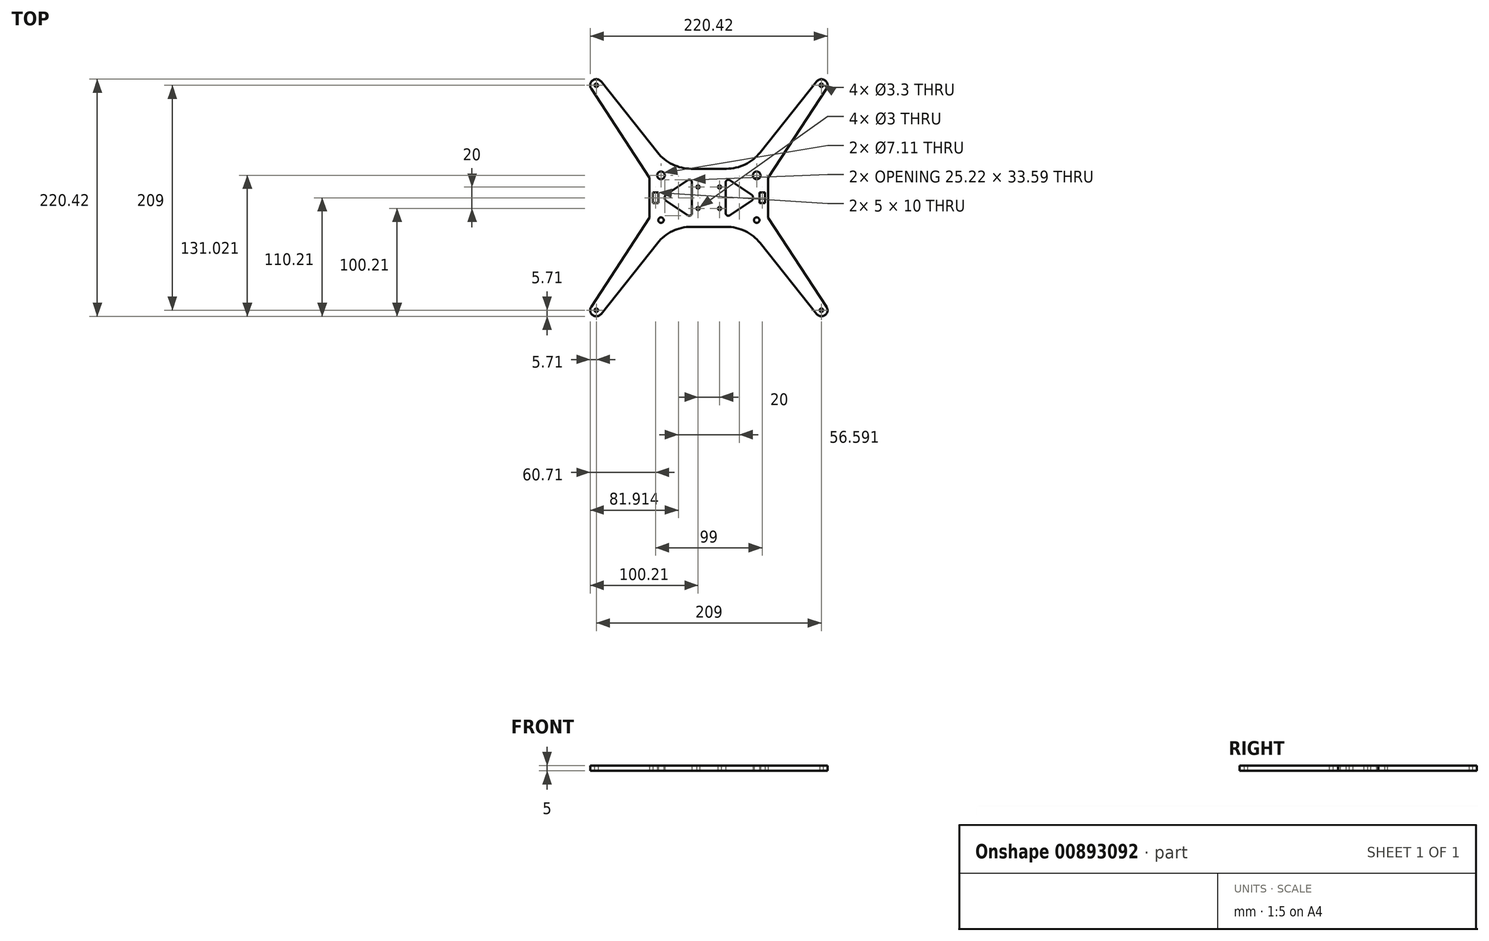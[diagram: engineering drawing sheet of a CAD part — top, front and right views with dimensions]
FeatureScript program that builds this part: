
annotation { "Feature Type Name" : "Feature", "Feature Type Description" : "" }
export const myFeature = defineFeature(function(context is Context, id is Id, definition is map)
    precondition{}
    {
        {
            var Q0;
            Q0=qCreatedBy(makeId("Top.planeOp"),FACE);
            var sketch = newSketch(context, id + "F0", { "sketchPlane" : qUnion([Q0])});
            skLineSegment(sketch, "E0", {"start": v(-39.8, -2.74) * mm, "end": v(-19.58, -16.37) * mm});
            skArc(sketch, "E1", {"start": v(-19.58, -16.37) * mm, "mid": v(-17.01, -16.5) * mm, "end": v(-15.68, -14.3) * mm});
            skLineSegment(sketch, "E2", {"start": v(-15.68, -14.3) * mm, "end": v(-15.68, 14.3) * mm});
            skArc(sketch, "E3", {"start": v(-15.68, 14.3) * mm, "mid": v(-17.01, 16.5) * mm, "end": v(-19.58, 16.37) * mm});
            skLineSegment(sketch, "E4", {"start": v(-19.58, 16.37) * mm, "end": v(-39.8, 2.74) * mm});
            skArc(sketch, "E5", {"start": v(-39.8, 2.74) * mm, "mid": v(-40.61, 1.84) * mm, "end": v(-40.9, 0.67) * mm});
            skLineSegment(sketch, "E6", {"start": v(-40.9, 0.67) * mm, "end": v(-40.9, -0.67) * mm});
            skArc(sketch, "E7", {"start": v(-40.9, -0.67) * mm, "mid": v(-40.61, -1.84) * mm, "end": v(-39.8, -2.74) * mm});
            skLineSegment(sketch, "E8", {"start": v(39.8, 2.74) * mm, "end": v(19.58, 16.37) * mm});
            skArc(sketch, "E9", {"start": v(19.58, 16.37) * mm, "mid": v(17.01, 16.5) * mm, "end": v(15.68, 14.3) * mm});
            skLineSegment(sketch, "E10", {"start": v(15.68, 14.3) * mm, "end": v(15.68, -14.3) * mm});
            skArc(sketch, "E11", {"start": v(15.68, -14.3) * mm, "mid": v(17.01, -16.5) * mm, "end": v(19.58, -16.37) * mm});
            skLineSegment(sketch, "E12", {"start": v(19.58, -16.37) * mm, "end": v(39.8, -2.74) * mm});
            skArc(sketch, "E13", {"start": v(39.8, -2.74) * mm, "mid": v(40.61, -1.84) * mm, "end": v(40.9, -0.67) * mm});
            skLineSegment(sketch, "E14", {"start": v(40.9, -0.67) * mm, "end": v(40.9, 0.67) * mm});
            skArc(sketch, "E15", {"start": v(40.9, 0.67) * mm, "mid": v(40.61, 1.84) * mm, "end": v(39.8, 2.74) * mm});
            skCircle(sketch, "E16", {"center": v(104.5, 104.5) * mm, "radius": 1.65 * mm});
            skCircle(sketch, "E17", {"center": v(44.44, 20.81) * mm, "radius": 3.56 * mm});
            skCircle(sketch, "E18", {"center": v(-104.5, 104.5) * mm, "radius": 1.65 * mm});
            skLineSegment(sketch, "E19", {"start": v(-100.03, 108.05) * mm, "end": v(-47.64, 42.12) * mm});
            skArc(sketch, "E20", {"start": v(-47.64, 42.12) * mm, "mid": v(-33.71, 30.98) * mm, "end": v(-16.32, 27) * mm});
            skLineSegment(sketch, "E21", {"start": v(-16.32, 27) * mm, "end": v(16.32, 27) * mm});
            skArc(sketch, "E22", {"start": v(16.32, 27) * mm, "mid": v(33.71, 30.98) * mm, "end": v(47.64, 42.12) * mm});
            skLineSegment(sketch, "E23", {"start": v(47.64, 42.12) * mm, "end": v(100.03, 108.05) * mm});
            skArc(sketch, "E24", {"start": v(100.03, 108.05) * mm, "mid": v(107.84, 109.12) * mm, "end": v(109.27, 101.37) * mm});
            skLineSegment(sketch, "E25", {"start": v(109.27, 101.37) * mm, "end": v(55, 18.66) * mm});
            skLineSegment(sketch, "E26", {"start": v(55, 18.66) * mm, "end": v(55, -18.66) * mm});
            skLineSegment(sketch, "E27", {"start": v(55, -18.66) * mm, "end": v(109.27, -101.37) * mm});
            skArc(sketch, "E28", {"start": v(109.27, -101.37) * mm, "mid": v(107.84, -109.12) * mm, "end": v(100.03, -108.05) * mm});
            skLineSegment(sketch, "E29", {"start": v(100.03, -108.05) * mm, "end": v(47.64, -42.12) * mm});
            skArc(sketch, "E30", {"start": v(47.64, -42.12) * mm, "mid": v(33.71, -30.98) * mm, "end": v(16.33, -27) * mm});
            skLineSegment(sketch, "E31", {"start": v(16.33, -27) * mm, "end": v(-16.33, -27) * mm});
            skArc(sketch, "E32", {"start": v(-16.33, -27) * mm, "mid": v(-33.71, -30.98) * mm, "end": v(-47.64, -42.12) * mm});
            skLineSegment(sketch, "E33", {"start": v(-47.64, -42.12) * mm, "end": v(-100.03, -108.05) * mm});
            skArc(sketch, "E34", {"start": v(-100.03, -108.05) * mm, "mid": v(-107.84, -109.12) * mm, "end": v(-109.27, -101.37) * mm});
            skLineSegment(sketch, "E35", {"start": v(-109.27, -101.37) * mm, "end": v(-55, -18.66) * mm});
            skLineSegment(sketch, "E36", {"start": v(-55, -18.66) * mm, "end": v(-55, 18.66) * mm});
            skLineSegment(sketch, "E37", {"start": v(-55, 18.66) * mm, "end": v(-109.27, 101.37) * mm});
            skArc(sketch, "E38", {"start": v(-109.27, 101.37) * mm, "mid": v(-107.84, 109.12) * mm, "end": v(-100.03, 108.05) * mm});
            skCircle(sketch, "E39", {"center": v(-44.44, 20.81) * mm, "radius": 3.56 * mm});
            skCircle(sketch, "E40", {"center": v(10, 10) * mm, "radius": 1.5 * mm});
            skCircle(sketch, "E41", {"center": v(-10, -10) * mm, "radius": 1.5 * mm});
            skCircle(sketch, "E42", {"center": v(10, -10) * mm, "radius": 1.5 * mm});
            skCircle(sketch, "E43", {"center": v(-10, 10) * mm, "radius": 1.5 * mm});
            skLineSegment(sketch, "E44", {"start": v(-52, -5) * mm, "end": v(-47, -5) * mm});
            skLineSegment(sketch, "E45", {"start": v(-47, -5) * mm, "end": v(-47, 5) * mm});
            skLineSegment(sketch, "E46", {"start": v(-47, 5) * mm, "end": v(-52, 5) * mm});
            skLineSegment(sketch, "E47", {"start": v(-52, 5) * mm, "end": v(-52, -5) * mm});
            skLineSegment(sketch, "E48", {"start": v(47, 5) * mm, "end": v(47, -5) * mm});
            skLineSegment(sketch, "E49", {"start": v(47, -5) * mm, "end": v(52, -5) * mm});
            skLineSegment(sketch, "E50", {"start": v(52, -5) * mm, "end": v(52, 5) * mm});
            skLineSegment(sketch, "E51", {"start": v(52, 5) * mm, "end": v(47, 5) * mm});
            skCircle(sketch, "E52", {"center": v(-44.44, -20.8) * mm, "radius": 2.55 * mm});
            skCircle(sketch, "E53", {"center": v(-104.5, -104.5) * mm, "radius": 1.65 * mm});
            skCircle(sketch, "E54", {"center": v(44.44, -20.8) * mm, "radius": 2.55 * mm});
            skCircle(sketch, "E55", {"center": v(104.5, -104.5) * mm, "radius": 1.65 * mm});
            skSolve(sketch);
        }
        {
            var Q0;
            Q0 = qSketchRegion(id + "F0", true);
            extrude(context, id + "F1", {"entities" : qUnion([Q0]), "depth" : 5 * mm, "offsetDistance" : 25 * mm});
        }
    });
